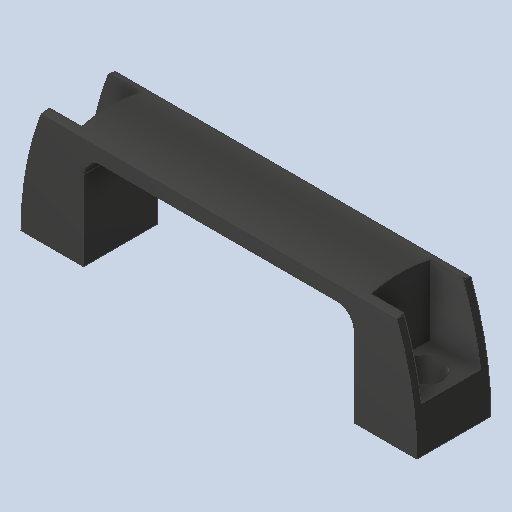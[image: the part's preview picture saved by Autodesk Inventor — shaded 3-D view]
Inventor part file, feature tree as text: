
AUTODESK INVENTOR PART (.ipt)
format: ipt  version: 2024.2 (Build 282272000, 272)  size: 186,368 bytes
history: native  units: mm
features: other x49, sketch x5, extrude x3, hole x2
ambient origin geometry x8: Origin, YZ Plane, XZ Plane, XY Plane, X Axis, Y Axis, Z Axis, Center Point
bodies: Solid1 (feature_tree)
feature tree (59):
  extrude  "Extrusion1"  Depth=58.5mm TaperAngle=0.0deg
  extrude  "Extrusion2"  Depth=139.0mm TaperAngle=0.0deg
  hole  "Hole1"  [1 undecoded]
  hole  "Hole2"  [1 undecoded]
  extrude  "Extrusion3"  [1 undecoded]
  other  "handle_to_body_XY"
  other  "handle_to_body_YZ"
  other  "handle_to_body_ZX"
  other  "handle_to_body_X"
  other  "handle_to_body_Y"
  other  "handle_to_body_Z"
  other  "handle_to_body_Center"
  other  "handle_to_bolt1_XY"
  other  "handle_to_bolt1_YZ"
  other  "handle_to_bolt1_ZX"
  other  "handle_to_bolt1_X"
  other  "handle_to_bolt1_Y"
  other  "handle_to_bolt1_Z"
  other  "handle_to_bolt1_Center"
  other  "handle_to_bolt2_XY"
  other  "handle_to_bolt2_YZ"
  other  "handle_to_bolt2_ZX"
  other  "handle_to_bolt2_X"
  other  "handle_to_bolt2_Y"
  other  "handle_to_bolt2_Z"
  other  "handle_to_bolt2_Center"
  other  "handle_to_nut1_XY"
  other  "handle_to_nut1_YZ"
  other  "handle_to_nut1_ZX"
  other  "handle_to_nut1_X"
  other  "handle_to_nut1_Y"
  other  "handle_to_nut1_Z"
  other  "handle_to_nut1_Center"
  other  "handle_to_nut2_XY"
  other  "handle_to_nut2_YZ"
  other  "handle_to_nut2_ZX"
  other  "handle_to_nut2_X"
  other  "handle_to_nut2_Y"
  other  "handle_to_nut2_Z"
  other  "handle_to_nut2_Center"
  other  "to_nut_1_XY"
  other  "to_nut_1_YZ"
  other  "to_nut_1_ZX"
  other  "to_nut_1_X"
  other  "to_nut_1_Y"
  other  "to_nut_1_Z"
  other  "to_nut_1_Center"
  other  "to_nut_2_XY"
  other  "to_nut_2_YZ"
  other  "to_nut_2_ZX"
  other  "to_nut_2_X"
  other  "to_nut_2_Y"
  other  "to_nut_2_Z"
  other  "to_nut_2_Center"
  sketch  "Sketch_1"  dims[d0=26.0mm d1=0.0mm d2=58.5mm d3=0.0mm]
  sketch  "Sketch_2"  dims[d4=8.5mm d5=6.0mm d6=13.3mm d7=9.0mm d8=90.0deg d9=15.0mm d10=0.0mm]
  sketch  "Sketch3"  dims[d11=8.5mm d12=6.0mm d13=13.3mm d14=9.0mm d15=90.0deg d16=15.0mm d17=0.0mm d18=139.0mm d19=0.0mm]
  sketch  "Sketch4"  dims[d20=0.0mm d21=0.0mm d22=0.0mm d23=0.0mm]
  sketch  "Sketch_6"
note: 3 required parameter values undecoded (feature->parameter linkage not recoverable at this tier; creation-order binding heuristic only, values carry confidence <= 0.55)
